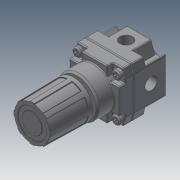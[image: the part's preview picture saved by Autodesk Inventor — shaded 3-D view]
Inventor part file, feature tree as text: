
AUTODESK INVENTOR PART (.ipt)
format: ipt  version: 2020.4 (Build 244396000, 396)  size: 1,496,576 bytes
history: native  units: in
note: dims shown in document units (in); Inventor stores cm internally (conversion verified against a paired STEP export)
features: imported_body x5, extrude x2, mirror x2, fillet x1, other x1, sketch x1
ambient origin geometry x8: Origin, YZ Plane, XZ Plane, XY Plane, X Axis, Y Axis, Z Axis, Center Point
bodies: Body1 (feature_tree), Body2 (feature_tree), Body3 (feature_tree), Body4 (feature_tree), Body5 (feature_tree)
feature tree (12):
  fillet  "Fillet3"  Radius=0.0197in
  extrude  "Extrusion1"  [1 undecoded]
  extrude  "Extrude5"  [1 undecoded]
  other  "Cut-Extrude3"
  mirror  "Mirror16"
  mirror  "Mirror19"
  sketch  "Sketch1"
  imported_body  "Base1"
  imported_body  "Base2"
  imported_body  "Base3"
  imported_body  "Base4"
  imported_body  "Base5"
note: 2 required parameter values undecoded (feature->parameter linkage not recoverable at this tier; creation-order binding heuristic only, values carry confidence <= 0.55)
